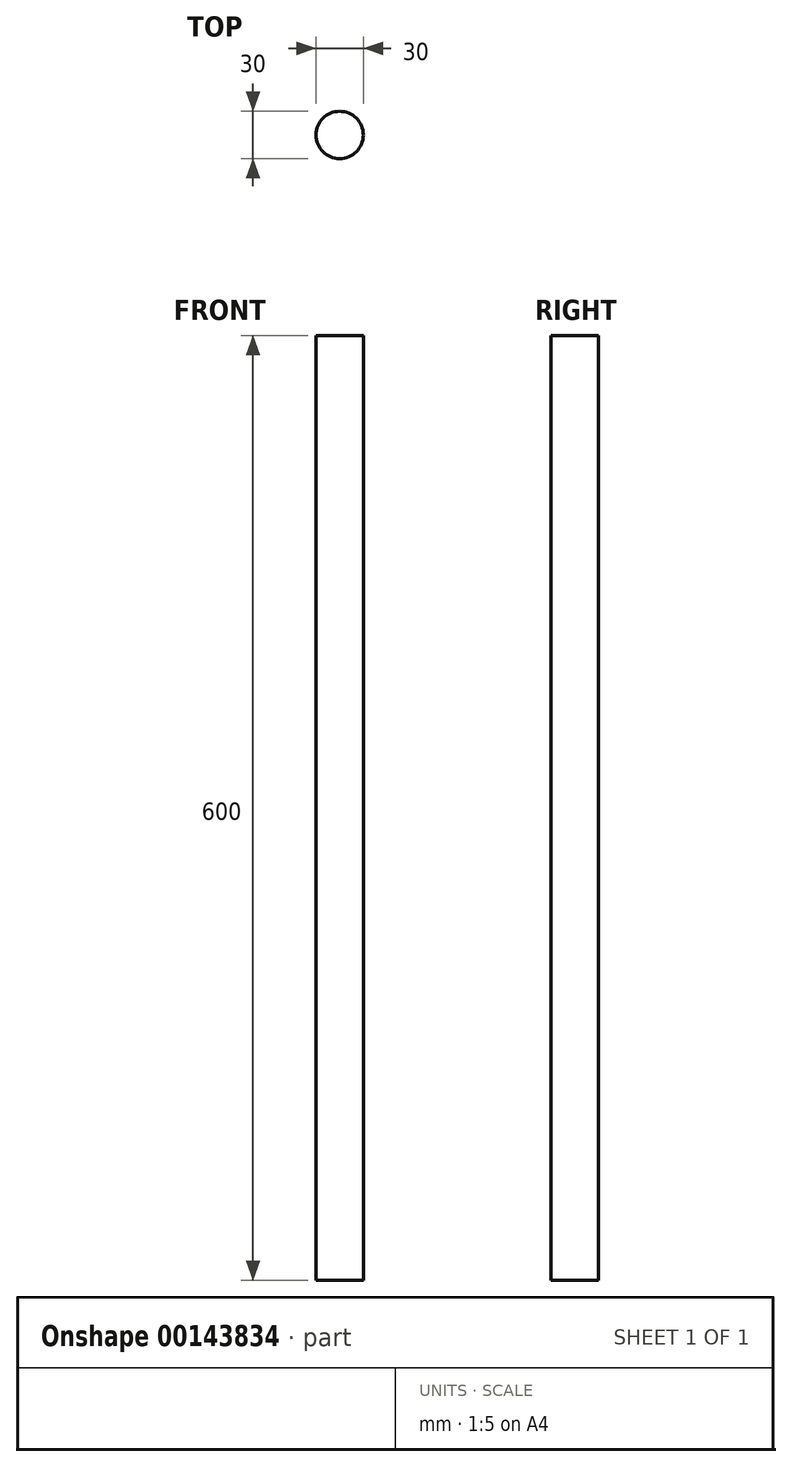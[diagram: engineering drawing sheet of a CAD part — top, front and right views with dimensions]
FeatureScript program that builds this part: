
annotation { "Feature Type Name" : "Feature", "Feature Type Description" : "" }
export const myFeature = defineFeature(function(context is Context, id is Id, definition is map)
    precondition{}
    {
        {
            var Q0;
            Q0=qCreatedBy(makeId("Top.planeOp"),FACE);
            var sketch = newSketch(context, id + "F0", { "sketchPlane" : qUnion([Q0])});
            skCircle(sketch, "E0", {"center": v(0, 0) * mm, "radius": 15 * mm});
            skSolve(sketch);
        }
        {
            var Q0;
            Q0=makeQuery(id+"F0.imprint","IMPRINT",FACE,{"disambiguationData":[TD([[makeQuery(id+"F0.imprint","IMPRINT",EDGE,{"derivedFrom":sQuery(id+"F0.wireOp",EDGE,"E0")}),1.0]])]});
            extrude(context, id + "F1", {"entities" : qUnion([Q0]), "depth" : 600 * mm});
        }
    });
